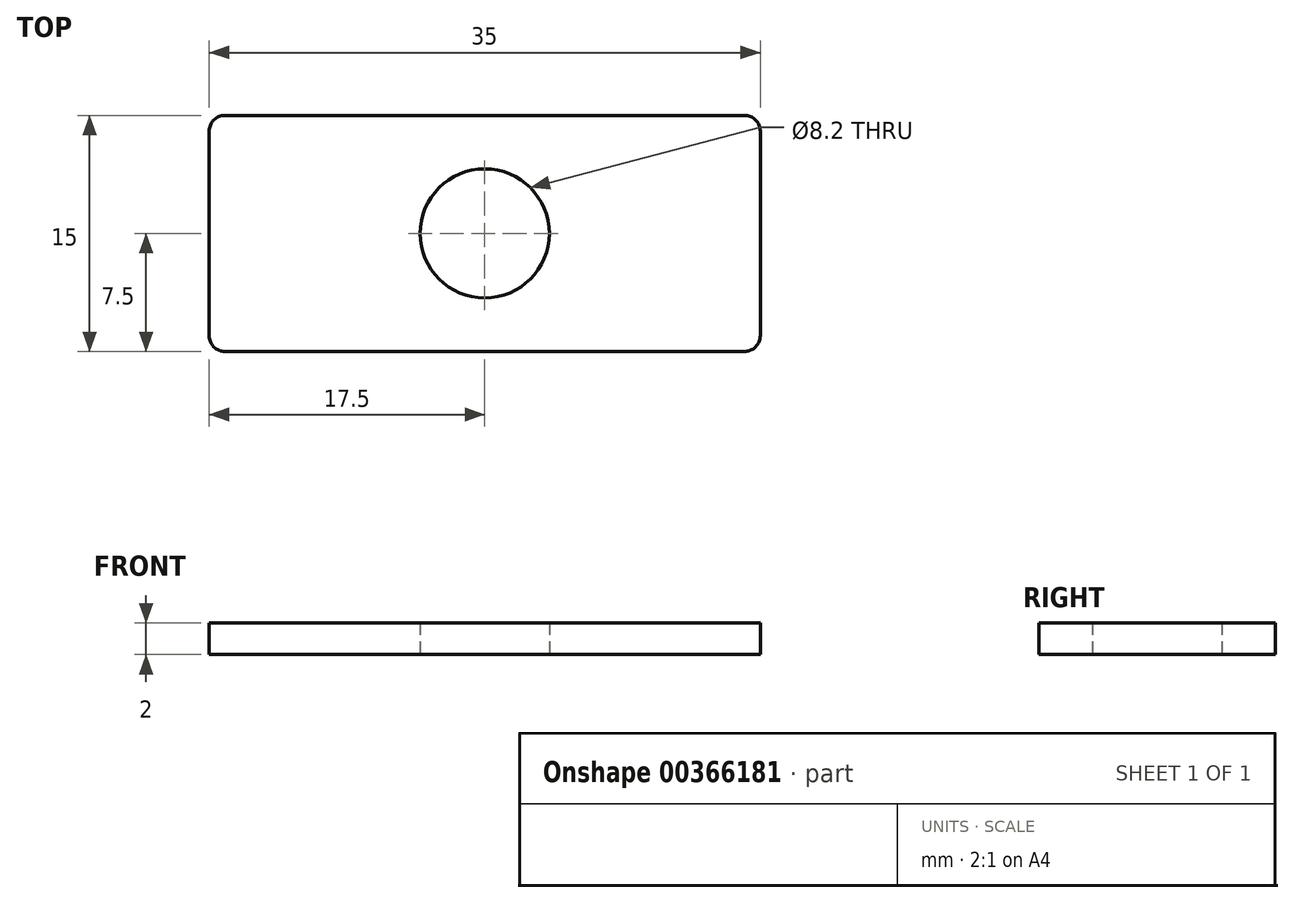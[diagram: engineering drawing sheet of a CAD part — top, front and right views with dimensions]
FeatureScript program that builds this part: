
annotation { "Feature Type Name" : "Feature", "Feature Type Description" : "" }
export const myFeature = defineFeature(function(context is Context, id is Id, definition is map)
    precondition{}
    {
        {
            var Q0;
            Q0=qCreatedBy(makeId("Top.planeOp"),FACE);
            var sketch = newSketch(context, id + "F0", { "sketchPlane" : qUnion([Q0])});
            skLineSegment(sketch, "E0.bottom", {"start": v(17.5, -7.5) * mm, "end": v(-17.5, -7.5) * mm});
            skLineSegment(sketch, "E0.top", {"start": v(17.5, 7.5) * mm, "end": v(-17.5, 7.5) * mm});
            skLineSegment(sketch, "E0.left", {"start": v(17.5, -7.5) * mm, "end": v(17.5, 7.5) * mm});
            skLineSegment(sketch, "E0.right", {"start": v(-17.5, -7.5) * mm, "end": v(-17.5, 7.5) * mm});
            skPoint(sketch, "E0.middle", {"position": v(0, 0) * mm});
            skCircle(sketch, "E1", {"center": v(0, 0) * mm, "radius": 4.1 * mm});
            skSolve(sketch);
        }
        {
            var Q0;
            Q0=makeQuery(id+"F0.imprint","IMPRINT",FACE,{"disambiguationData":[TD([[makeQuery(id+"F0.imprint","IMPRINT",EDGE,{"derivedFrom":sQuery(id+"F0.wireOp",EDGE,"E0.bottom")}),-1.0]])]});
            extrude(context, id + "F1", {"entities" : qUnion([Q0]), "depth" : 2 * mm});
        }
        {
            var Q0;
            Q0=makeQuery(id+"F1.opExtrude","SWEPT_EDGE",EDGE,{"disambiguationData":[OSD([sQuery(id+"F0.wireOp",EDGE,"E0.top"),sQuery(id+"F0.wireOp",EDGE,"E0.right")])]});
            var Q1;
            Q1=makeQuery(id+"F1.opExtrude","SWEPT_EDGE",EDGE,{"disambiguationData":[OSD([sQuery(id+"F0.wireOp",EDGE,"E0.top"),sQuery(id+"F0.wireOp",EDGE,"E0.left")])]});
            var Q2;
            Q2=makeQuery(id+"F1.opExtrude","SWEPT_EDGE",EDGE,{"disambiguationData":[OSD([sQuery(id+"F0.wireOp",EDGE,"E0.bottom"),sQuery(id+"F0.wireOp",EDGE,"E0.left")])]});
            var Q3;
            Q3=makeQuery(id+"F1.opExtrude","SWEPT_EDGE",EDGE,{"disambiguationData":[OSD([sQuery(id+"F0.wireOp",EDGE,"E0.bottom"),sQuery(id+"F0.wireOp",EDGE,"E0.right")])]});
            fillet(context, id + "F2", {"entities" : qUnion([Q0, Q1, Q2, Q3]), "radius" : 1 * mm, "tangentPropagation" : true, "allowEdgeOverflow" : false});
        }
    });
